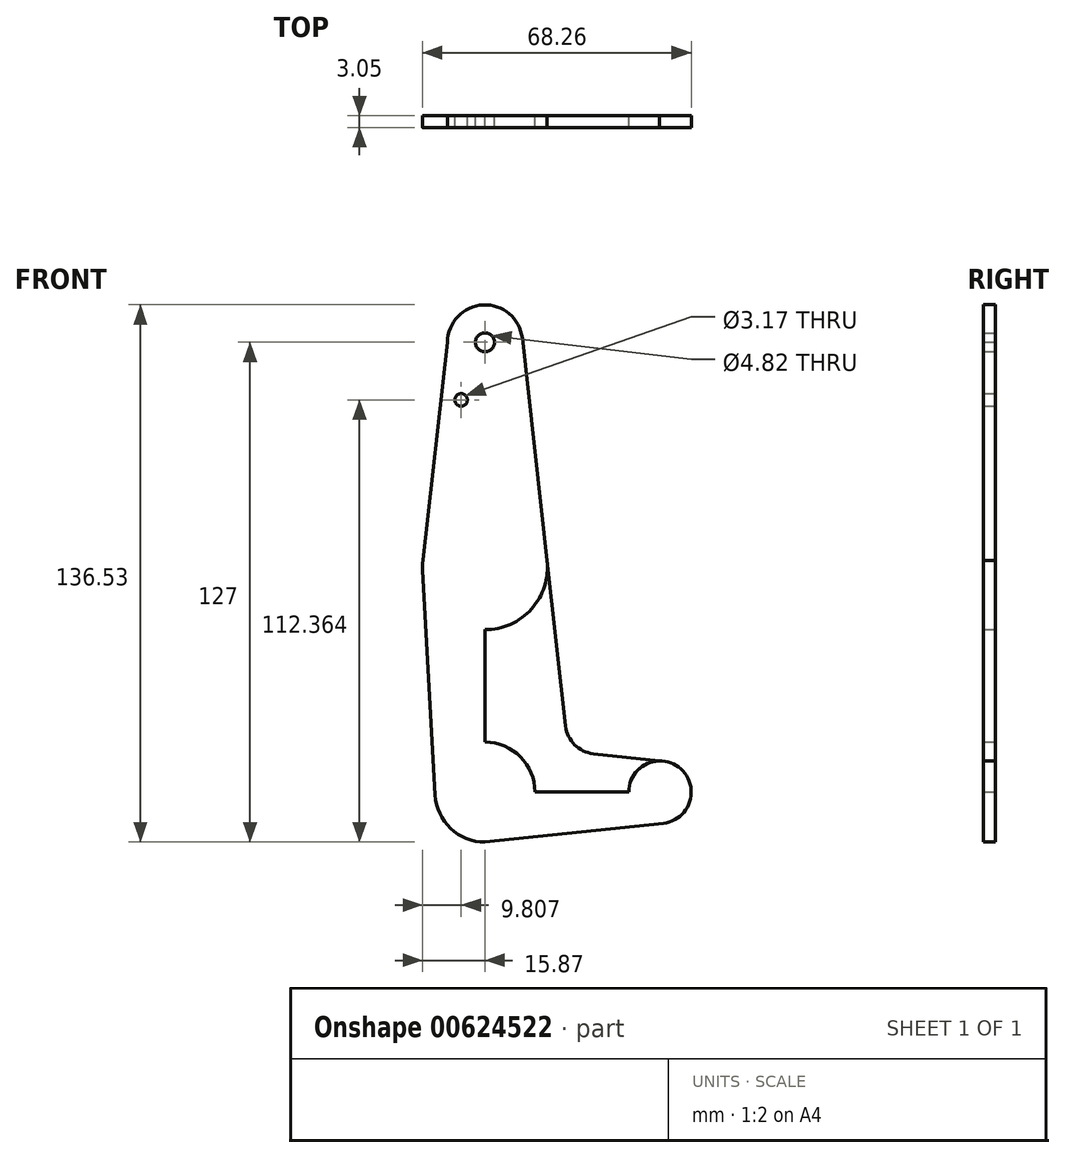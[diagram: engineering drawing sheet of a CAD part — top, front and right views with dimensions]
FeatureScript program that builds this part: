
annotation { "Feature Type Name" : "Feature", "Feature Type Description" : "" }
export const myFeature = defineFeature(function(context is Context, id is Id, definition is map)
    precondition{}
    {
        {
            var Q0;
            Q0=qCreatedBy(makeId("Front.planeOp"),FACE);
            var sketch = newSketch(context, id + "F0", { "sketchPlane" : qUnion([Q0])});
            skLineSegment(sketch, "E0", {"start": v(0, 0) * mm, "end": v(0, 114.3) * mm, "construction": true});
            skLineSegment(sketch, "E1", {"start": v(0, 0) * mm, "end": v(44.45, 0) * mm});
            skCircle(sketch, "E2", {"center": v(0, 114.3) * mm, "radius": 9.53 * mm});
            skCircle(sketch, "E3", {"center": v(0, 57.15) * mm, "radius": 15.88 * mm});
            skCircle(sketch, "E4", {"center": v(0, 0) * mm, "radius": 12.7 * mm});
            skCircle(sketch, "E5", {"center": v(44.45, 0) * mm, "radius": 7.94 * mm});
            skLineSegment(sketch, "E6", {"start": v(0, 57.15) * mm, "end": v(0, 0) * mm});
            skCircle(sketch, "E7", {"center": v(-6.06, 99.66) * mm, "radius": 1.59 * mm});
            skLineSegment(sketch, "E8", {"start": v(-9.52, 114.33) * mm, "end": v(-15.77, 58.93) * mm});
            skLineSegment(sketch, "E9", {"start": v(0, -12.7) * mm, "end": v(48.03, -7.6) * mm});
            skLineSegment(sketch, "E10", {"start": v(44.33, 7.94) * mm, "end": v(27.52, 9.77) * mm});
            skLineSegment(sketch, "E11", {"start": v(20.49, 16.8) * mm, "end": v(15.78, 58.91) * mm});
            skLineSegment(sketch, "E12", {"start": v(15.78, 58.91) * mm, "end": v(9.47, 115.36) * mm});
            skCircle(sketch, "E13", {"center": v(0, 114.3) * mm, "radius": 2.4 * mm});
            skArc(sketch, "E14.filletArc", {"start": v(20.49, 16.8) * mm, "mid": v(22.77, 12.05) * mm, "end": v(27.52, 9.77) * mm});
            skLineSegment(sketch, "E15", {"start": v(-15.85, 56.27) * mm, "end": v(-12.68, -0.7) * mm});
            skSolve(sketch);
        }
        {
            var Q0;
            {var subQ0=sQuery(id+"F0.wireOp",EDGE,"E15");Q0=makeQuery(id+"F0.imprint","IMPRINT",FACE,{"disambiguationData":[TD([[makeQuery(id+"F0.imprint","IMPRINT",EDGE,{"derivedFrom":subQ0}),1.0]])]});}
            var Q1;
            {var subQ3=sQuery(id+"F0.wireOp",EDGE,"E1");var subQ7=sQuery(id+"F0.wireOp",EDGE,"E6");var subQ9=makeQuery(id+"F0.imprint","INTERSECT",VERTEX,{"derivedFrom":[subQ3,subQ7]});Q1=makeQuery(id+"F0.imprint","IMPRINT",FACE,{"disambiguationData":[TD([[makeQuery(id+"F0.imprint","IMPRINT",EDGE,{"disambiguationData":[TD([[subQ9,-1.0]])],"derivedFrom":subQ3}),-1.0]])]});}
            var Q2;
            {var subQ0=sQuery(id+"F0.wireOp",EDGE,"E6");var subQ1=sQuery(id+"F0.wireOp",EDGE,"E1");var subQ2=makeQuery(id+"F0.imprint","INTERSECT",VERTEX,{"derivedFrom":[subQ1,subQ0]});Q2=makeQuery(id+"F0.imprint","IMPRINT",FACE,{"disambiguationData":[TD([[makeQuery(id+"F0.imprint","IMPRINT",EDGE,{"disambiguationData":[TD([[subQ2,-1.0]])],"derivedFrom":subQ1}),1.0]])]});}
            var Q3;
            {var subQ0=sQuery(id+"F0.wireOp",EDGE,"E5");var subQ1=sQuery(id+"F0.wireOp",EDGE,"E1");var subQ2=makeQuery(id+"F0.imprint","INTERSECT",VERTEX,{"derivedFrom":[subQ1,subQ0]});Q3=makeQuery(id+"F0.imprint","IMPRINT",FACE,{"disambiguationData":[TD([[makeQuery(id+"F0.imprint","IMPRINT",EDGE,{"disambiguationData":[TD([[subQ2,1.0]])],"derivedFrom":subQ1}),-1.0]])]});}
            var Q4;
            {var subQ0=sQuery(id+"F0.wireOp",EDGE,"E5");var subQ1=makeQuery(id+"F0.imprint","INTERSECT",VERTEX,{"derivedFrom":[subQ0,sQuery(id+"F0.wireOp",EDGE,"E10")]});Q4=makeQuery(id+"F0.imprint","IMPRINT",FACE,{"disambiguationData":[TD([[makeQuery(id+"F0.imprint","IMPRINT",EDGE,{"disambiguationData":[TD([[subQ1,-1.0]])],"derivedFrom":subQ0}),1.0]])]});}
            var Q5;
            {var subQ1=sQuery(id+"F0.wireOp",EDGE,"E3");var subQ5=sQuery(id+"F0.wireOp",EDGE,"E8");var subQ7=makeQuery(id+"F0.imprint","INTERSECT",VERTEX,{"disambiguationData":[OD(1.0)],"derivedFrom":[subQ1,subQ5]});Q5=makeQuery(id+"F0.imprint","IMPRINT",FACE,{"disambiguationData":[TD([[makeQuery(id+"F0.imprint","IMPRINT",EDGE,{"disambiguationData":[TD([[subQ7,1.0]])],"derivedFrom":subQ1}),1.0]])]});}
            var Q6;
            Q6=makeQuery(id+"F0.imprint","IMPRINT",FACE,{"disambiguationData":[TD([[makeQuery(id+"F0.imprint","IMPRINT",EDGE,{"derivedFrom":sQuery(id+"F0.wireOp",EDGE,"E7")}),-1.0]])]});
            var Q7;
            Q7=makeQuery(id+"F0.imprint","IMPRINT",FACE,{"disambiguationData":[TD([[makeQuery(id+"F0.imprint","IMPRINT",EDGE,{"derivedFrom":sQuery(id+"F0.wireOp",EDGE,"E13")}),-1.0]])]});
            extrude(context, id + "F1", {"entities" : qUnion([Q0, Q1, Q2, Q3, Q4, Q5, Q6, Q7]), "depth" : 3.05 * mm, "offsetDistance" : 25.4 * mm});
        }
        {
            var Q0;
            {var subQ0=sQuery(id+"F0.wireOp",EDGE,"E10");Q0=makeQuery(id+"F0.imprint","IMPRINT",FACE,{"disambiguationData":[TD([[makeQuery(id+"F0.imprint","IMPRINT",EDGE,{"derivedFrom":subQ0}),1.0]])]});}
            extrude(context, id + "F2", {"entities" : qUnion([Q0]), "depth" : 3.05 * mm, "offsetDistance" : 25.4 * mm});
        }
    });
